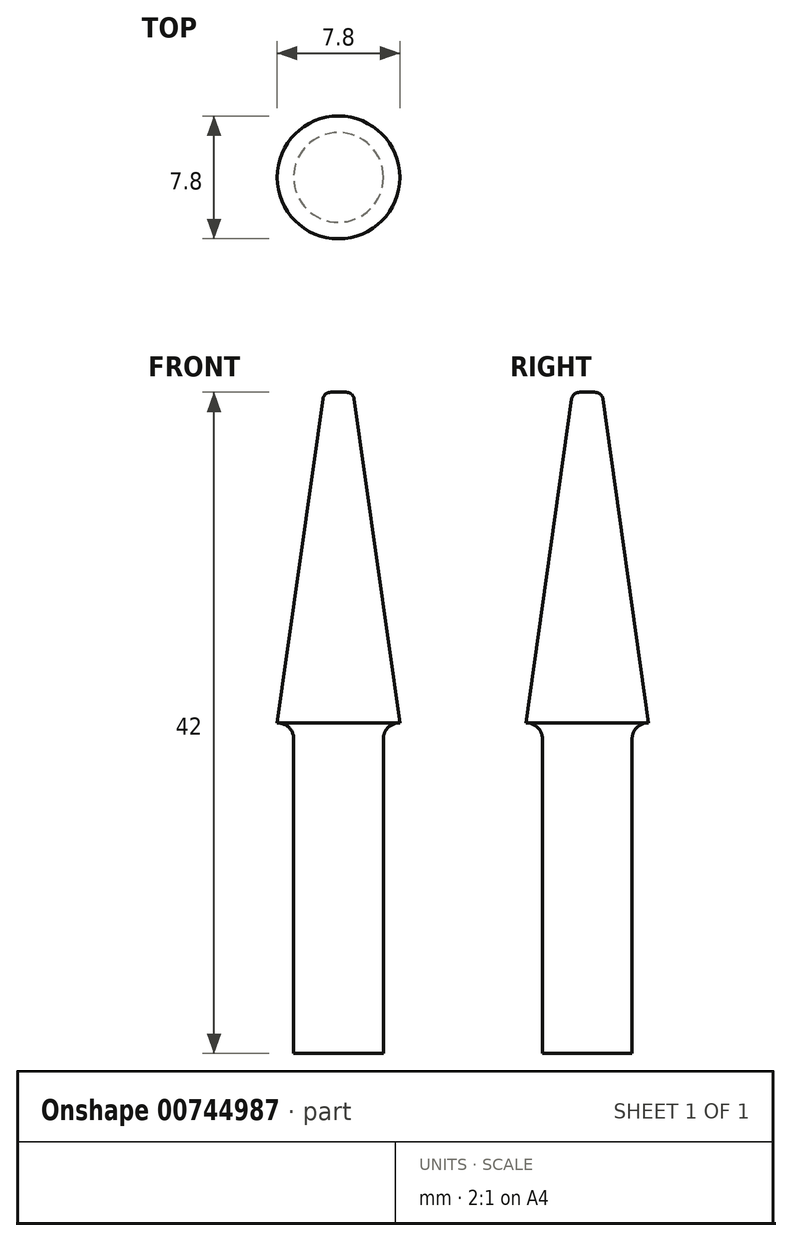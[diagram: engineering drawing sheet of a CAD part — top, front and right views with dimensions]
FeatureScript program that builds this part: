
annotation { "Feature Type Name" : "Feature", "Feature Type Description" : "" }
export const myFeature = defineFeature(function(context is Context, id is Id, definition is map)
    precondition{}
    {
        {
            var Q0;
            Q0=qCreatedBy(makeId("Front.planeOp"),FACE);
            var sketch = newSketch(context, id + "F0", { "sketchPlane" : qUnion([Q0])});
            skLineSegment(sketch, "E0", {"start": v(1, 41.57) * mm, "end": v(3.9, 21) * mm});
            skLineSegment(sketch, "E1", {"start": v(2.85, 20) * mm, "end": v(2.85, 0) * mm});
            skLineSegment(sketch, "E2", {"start": v(2.85, 0) * mm, "end": v(0, 0) * mm});
            skLineSegment(sketch, "E3", {"start": v(0, 0) * mm, "end": v(0, 42) * mm});
            skPoint(sketch, "E4.endSnap0", {"position": v(0, 21) * mm});
            skLineSegment(sketch, "E5", {"start": v(0.5, 42) * mm, "end": v(0, 42) * mm});
            skPoint(sketch, "E6.visualSharp", {"position": v(0.93, 42) * mm});
            skArc(sketch, "E6.filletArc", {"start": v(1, 41.57) * mm, "mid": v(0.83, 41.88) * mm, "end": v(0.5, 42) * mm});
            skLineSegment(sketch, "E7", {"start": v(3.85, 21) * mm, "end": v(3.9, 21) * mm});
            skPoint(sketch, "E8.visualSharp", {"position": v(2.85, 21) * mm});
            skArc(sketch, "E8.filletArc", {"start": v(3.85, 21) * mm, "mid": v(3.14, 20.7) * mm, "end": v(2.85, 20) * mm});
            skSolve(sketch);
        }
        {
            var Q0;
            {var subQ0=sQuery(id+"F0.wireOp",EDGE,"E0");Q0=makeQuery(id+"F0.imprint","IMPRINT",FACE,{"disambiguationData":[TD([[makeQuery(id+"F0.imprint","IMPRINT",EDGE,{"derivedFrom":subQ0}),-1.0]])]});}
            var Q1;
            Q1=sQuery(id+"F0.wireOp",EDGE,"E3");
            revolve(context, id + "F1", {"surfaceOperationType" : NewSurfaceOperationType.NEW, "entities" : qUnion([Q0]), "axis" : qUnion([Q1]), "revolveType" : RevolveType.FULL});
        }
    });
